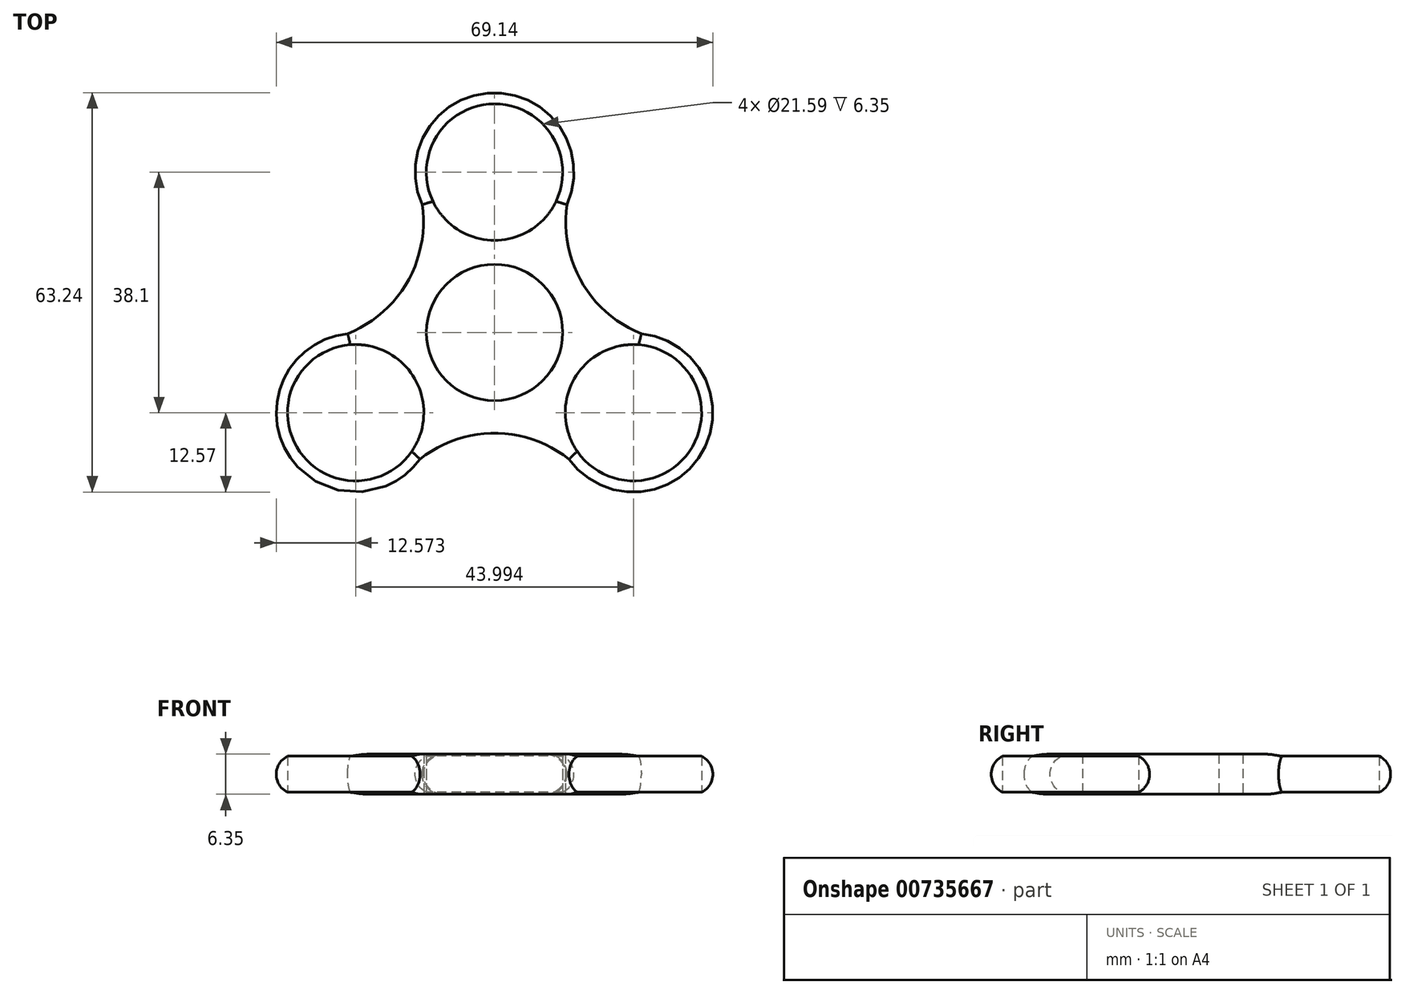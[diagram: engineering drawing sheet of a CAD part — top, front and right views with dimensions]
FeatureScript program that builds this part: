
annotation { "Feature Type Name" : "Feature", "Feature Type Description" : "" }
export const myFeature = defineFeature(function(context is Context, id is Id, definition is map)
    precondition{}
    {
        {
            var Q0;
            Q0=qCreatedBy(makeId("Top.planeOp"),FACE);
            var sketch = newSketch(context, id + "F0", { "sketchPlane" : qUnion([Q0])});
            skCircle(sketch, "E0", {"center": v(0, 0) * mm, "radius": 10.8 * mm});
            skLineSegment(sketch, "E1", {"start": v(0, 0) * mm, "end": v(0, 25.4) * mm});
            skCircle(sketch, "E2", {"center": v(0, 25.4) * mm, "radius": 10.8 * mm});
            skArc(sketch, "E3", {"start": v(11.47, 20.24) * mm, "mid": v(0, 37.97) * mm, "end": v(-11.47, 20.24) * mm});
            skArc(sketch, "E4.1.0", {"start": v(-23.26, -0.2) * mm, "mid": v(-32.89, -18.99) * mm, "end": v(-11.8, -20.05) * mm});
            skArc(sketch, "E4.2.0", {"start": v(11.8, -20.05) * mm, "mid": v(32.89, -18.99) * mm, "end": v(23.26, -0.2) * mm});
            skCircle(sketch, "E5.1.0", {"center": v(-22, -12.7) * mm, "radius": 10.8 * mm});
            skCircle(sketch, "E5.2.0", {"center": v(22, -12.7) * mm, "radius": 10.8 * mm});
            skLineSegment(sketch, "E6", {"start": v(-9.35, 5.4) * mm, "end": v(-10.89, 6.29) * mm});
            skPoint(sketch, "E7.center.orphan", {"position": v(-30.32, 17.5) * mm});
            skArc(sketch, "E8", {"start": v(-29.7, -2.76) * mm, "mid": v(-27.5, -1.77) * mm, "end": v(-25.4, -0.6) * mm});
            skArc(sketch, "E9.trimOffspring", {"start": v(-12.18, 22.29) * mm, "mid": v(-12.22, 24.7) * mm, "end": v(-12.46, 27.1) * mm});
            skArc(sketch, "E10", {"start": v(-27.32, -1.3) * mm, "mid": v(-13.82, 7.98) * mm, "end": v(-12.53, 24.31) * mm});
            skArc(sketch, "E11.1.0", {"start": v(14.8, -23) * mm, "mid": v(0, -15.96) * mm, "end": v(-14.8, -23) * mm});
            skArc(sketch, "E11.2.0", {"start": v(12.53, 24.31) * mm, "mid": v(13.82, 7.98) * mm, "end": v(27.32, -1.3) * mm});
            skPoint(sketch, "E12.orphan", {"position": v(-60.65, 35.01) * mm});
            skSolve(sketch);
        }
        {
            var Q0;
            Q0 = qSketchRegion(id + "F0", true);
            extrude(context, id + "F1", {"entities" : qUnion([Q0]), "depth" : 6.35 * mm, "offsetDistance" : 25.4 * mm});
        }
        {
            var Q0;
            Q0=makeQuery(id+"F1.opExtrude","CAP_EDGE",EDGE,{"disambiguationData":[OSD([sQuery(id+"F0.wireOp",EDGE,"E11.1.0")])],"isStart":true});
            var Q1;
            Q1=makeQuery(id+"F1.opExtrude","CAP_EDGE",EDGE,{"disambiguationData":[OSD([sQuery(id+"F0.wireOp",EDGE,"E4.1.0")])],"isStart":true});
            var Q2;
            Q2=makeQuery(id+"F1.opExtrude","CAP_EDGE",EDGE,{"disambiguationData":[OSD([sQuery(id+"F0.wireOp",EDGE,"E10")])],"isStart":true});
            var Q3;
            Q3=makeQuery(id+"F1.opExtrude","CAP_EDGE",EDGE,{"disambiguationData":[OSD([sQuery(id+"F0.wireOp",EDGE,"E3")])],"isStart":true});
            var Q4;
            Q4=makeQuery(id+"F1.opExtrude","CAP_EDGE",EDGE,{"disambiguationData":[OSD([sQuery(id+"F0.wireOp",EDGE,"E11.2.0")])],"isStart":true});
            var Q5;
            Q5=makeQuery(id+"F1.opExtrude","CAP_EDGE",EDGE,{"disambiguationData":[OSD([sQuery(id+"F0.wireOp",EDGE,"E4.2.0")])],"isStart":true});
            var Q6;
            Q6=makeQuery(id+"F1.opExtrude","CAP_EDGE",EDGE,{"disambiguationData":[OSD([sQuery(id+"F0.wireOp",EDGE,"E4.2.0")])],"isStart":false});
            var Q7;
            Q7=makeQuery(id+"F1.opExtrude","CAP_EDGE",EDGE,{"disambiguationData":[OSD([sQuery(id+"F0.wireOp",EDGE,"E11.1.0")])],"isStart":false});
            var Q8;
            Q8=makeQuery(id+"F1.opExtrude","CAP_EDGE",EDGE,{"disambiguationData":[OSD([sQuery(id+"F0.wireOp",EDGE,"E4.1.0")])],"isStart":false});
            var Q9;
            Q9=makeQuery(id+"F1.opExtrude","CAP_EDGE",EDGE,{"disambiguationData":[OSD([sQuery(id+"F0.wireOp",EDGE,"E10")])],"isStart":false});
            var Q10;
            Q10=makeQuery(id+"F1.opExtrude","CAP_EDGE",EDGE,{"disambiguationData":[OSD([sQuery(id+"F0.wireOp",EDGE,"E3")])],"isStart":false});
            var Q11;
            Q11=makeQuery(id+"F1.opExtrude","CAP_EDGE",EDGE,{"disambiguationData":[OSD([sQuery(id+"F0.wireOp",EDGE,"E11.2.0")])],"isStart":false});
            fillet(context, id + "F2", {"entities" : qUnion([Q0, Q1, Q2, Q3, Q4, Q5, Q6, Q7, Q8, Q9, Q10, Q11]), "radius" : 3.17 * mm, "tangentPropagation" : true, "allowEdgeOverflow" : false});
        }
    });
